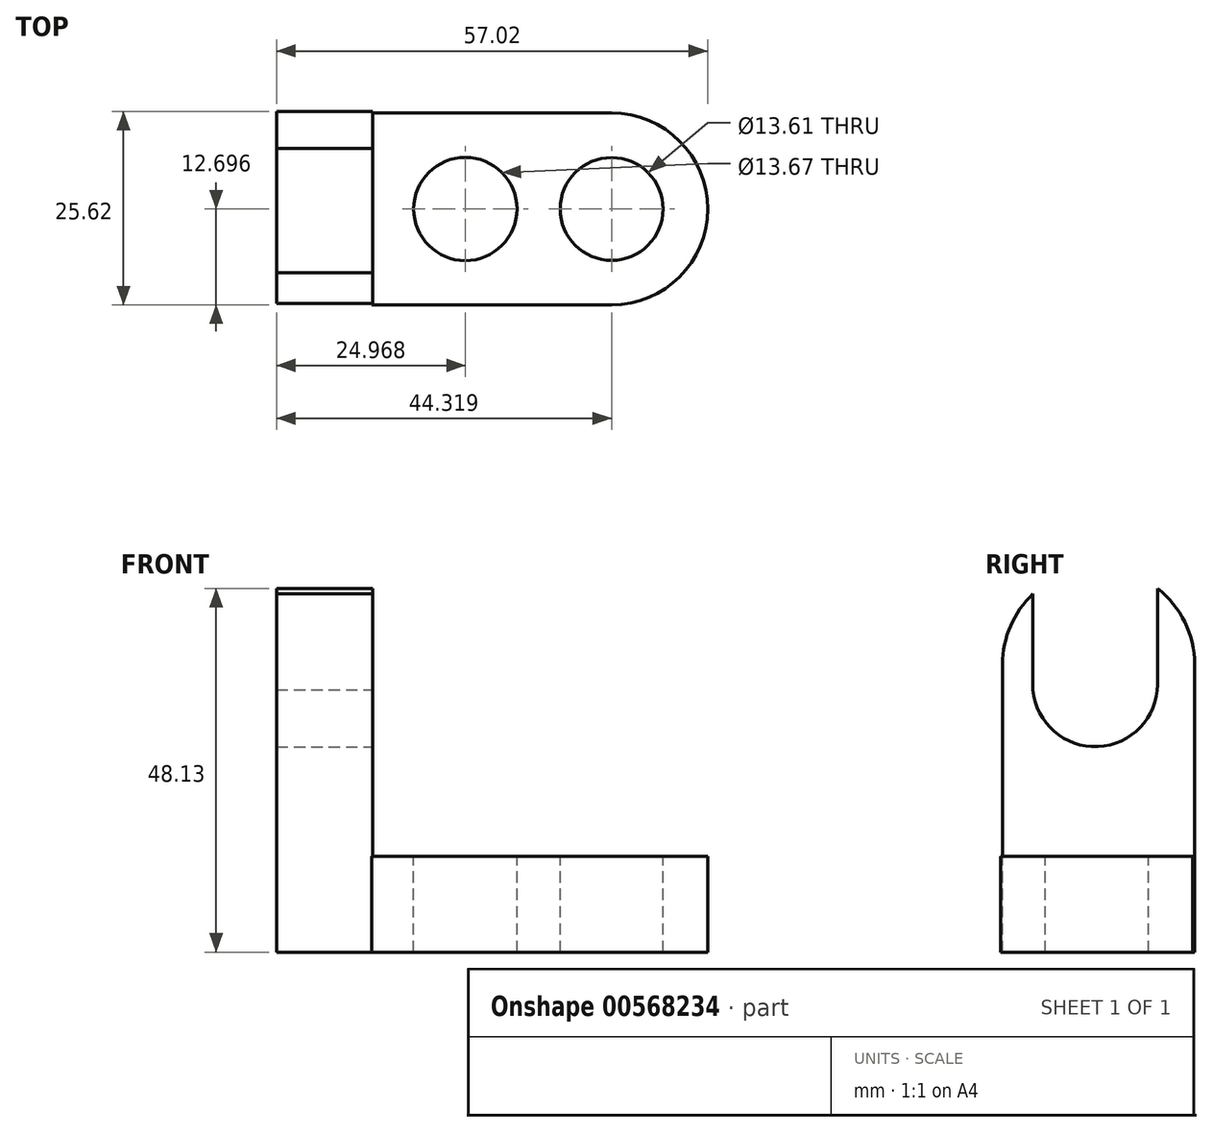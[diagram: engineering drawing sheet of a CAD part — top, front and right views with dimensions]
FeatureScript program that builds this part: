
annotation { "Feature Type Name" : "Feature", "Feature Type Description" : "" }
export const myFeature = defineFeature(function(context is Context, id is Id, definition is map)
    precondition{}
    {
        {
            var Q0;
            Q0=qCreatedBy(makeId("Right.planeOp"),FACE);
            var sketch = newSketch(context, id + "F0", { "sketchPlane" : qUnion([Q0])});
            skLineSegment(sketch, "E0", {"start": v(-51.63, 0) * mm, "end": v(-26.23, 0) * mm});
            skLineSegment(sketch, "E1", {"start": v(-26.23, 0) * mm, "end": v(-26.23, 38.1) * mm});
            skLineSegment(sketch, "E2", {"start": v(-26.23, 38.1) * mm, "end": v(-51.63, 38.1) * mm});
            skLineSegment(sketch, "E3", {"start": v(-51.63, 38.1) * mm, "end": v(-51.63, 0) * mm});
            skArc(sketch, "E4", {"start": v(-26.23, 38.1) * mm, "mid": v(-38.93, 50.8) * mm, "end": v(-51.63, 38.1) * mm});
            skSolve(sketch);
        }
        {
            var Q0;
            Q0=makeQuery(id+"F0.imprint","IMPRINT",FACE,{"disambiguationData":[TD([[makeQuery(id+"F0.imprint","IMPRINT",EDGE,{"derivedFrom":sQuery(id+"F0.wireOp",EDGE,"E0")}),1.0]])]});
            var Q1;
            Q1=makeQuery(id+"F0.imprint","IMPRINT",FACE,{"disambiguationData":[TD([[makeQuery(id+"F0.imprint","IMPRINT",EDGE,{"derivedFrom":sQuery(id+"F0.wireOp",EDGE,"E2")}),-1.0]])]});
            extrude(context, id + "F1", {"entities" : qUnion([Q0, Q1]), "depth" : 12.7 * mm, "offsetDistance" : 25.4 * mm});
        }
        {
            var Q0;
            Q0=qCreatedBy(makeId("Top.planeOp"),FACE);
            var sketch = newSketch(context, id + "F2", { "sketchPlane" : qUnion([Q0])});
            skLineSegment(sketch, "E5", {"start": v(12.57, -26.45) * mm, "end": v(44.32, -26.45) * mm});
            skLineSegment(sketch, "E6", {"start": v(44.32, -26.45) * mm, "end": v(44.32, -51.85) * mm});
            skLineSegment(sketch, "E7", {"start": v(44.32, -51.85) * mm, "end": v(12.57, -51.85) * mm});
            skLineSegment(sketch, "E8", {"start": v(12.57, -51.85) * mm, "end": v(12.57, -26.45) * mm});
            skArc(sketch, "E9", {"start": v(44.32, -51.85) * mm, "mid": v(57.02, -39.15) * mm, "end": v(44.32, -26.45) * mm});
            skSolve(sketch);
        }
        {
            var Q0;
            Q0=makeQuery(id+"F2.imprint","IMPRINT",FACE,{"disambiguationData":[TD([[makeQuery(id+"F2.imprint","IMPRINT",EDGE,{"derivedFrom":sQuery(id+"F2.wireOp",EDGE,"E6")}),1.0]])]});
            var Q1;
            Q1=makeQuery(id+"F2.imprint","IMPRINT",FACE,{"disambiguationData":[TD([[makeQuery(id+"F2.imprint","IMPRINT",EDGE,{"derivedFrom":sQuery(id+"F2.wireOp",EDGE,"E5")}),-1.0]])]});
            extrude(context, id + "F3", {"entities" : qUnion([Q0, Q1]), "operationType" : NewBodyOperationType.ADD, "depth" : 12.7 * mm, "offsetDistance" : 25.4 * mm});
        }
        {
            var Q0;
            Q0=makeQuery(id+"F1.opExtrude","CAP_FACE",FACE,{"disambiguationData":[OSD([sQuery(id+"F0.wireOp",EDGE,"E0"),sQuery(id+"F0.wireOp",EDGE,"E1"),sQuery(id+"F0.wireOp",EDGE,"E3"),sQuery(id+"F0.wireOp",EDGE,"E4")])],"isStart":false});
            var sketch = newSketch(context, id + "F4", { "sketchPlane" : qUnion([Q0])});
            skLineSegment(sketch, "E10", {"start": v(-47.6, 47.38) * mm, "end": v(-47.6, 34.68) * mm});
            skLineSegment(sketch, "E11", {"start": v(-31.14, 48.13) * mm, "end": v(-31.14, 35.43) * mm});
            skArc(sketch, "E12", {"start": v(-47.6, 34.68) * mm, "mid": v(-39, 27.2) * mm, "end": v(-31.14, 35.43) * mm});
            skArc(sketch, "E13", {"start": v(-31.14, 48.13) * mm, "mid": v(-39.76, 56.37) * mm, "end": v(-47.6, 47.38) * mm});
            skSolve(sketch);
        }
        {
            var Q0;
            {var subQ0=sQuery(id+"F4.wireOp",EDGE,"E13");Q0=makeQuery(id+"F4.imprint","IMPRINT",FACE,{"disambiguationData":[TD([[makeQuery(id+"F4.imprint","IMPRINT",EDGE,{"derivedFrom":subQ0}),1.0]])]});}
            var Q1;
            {var subQ0=sQuery(id+"F4.wireOp",EDGE,"E10");Q1=makeQuery(id+"F4.imprint","IMPRINT",FACE,{"disambiguationData":[TD([[makeQuery(id+"F4.imprint","IMPRINT",EDGE,{"derivedFrom":subQ0}),1.0]])]});}
            extrude(context, id + "F5", {"entities" : qUnion([Q0, Q1]), "operationType" : NewBodyOperationType.REMOVE, "oppositeDirection" : true, "depth" : 12.7 * mm, "offsetDistance" : 25.4 * mm});
        }
        {
            var Q0;
            Q0=makeQuery(id+"F3.opExtrude","CAP_FACE",FACE,{"disambiguationData":[OSD([sQuery(id+"F2.wireOp",EDGE,"E5"),sQuery(id+"F2.wireOp",EDGE,"E7"),sQuery(id+"F2.wireOp",EDGE,"E8"),sQuery(id+"F2.wireOp",EDGE,"E9")])],"isStart":false});
            var sketch = newSketch(context, id + "F6", { "sketchPlane" : qUnion([Q0])});
            skCircle(sketch, "E14", {"center": v(44.32, -39.15) * mm, "radius": 6.8 * mm});
            skCircle(sketch, "E15", {"center": v(24.97, -39.15) * mm, "radius": 6.83 * mm});
            skSolve(sketch);
        }
        {
            var Q0;
            Q0=makeQuery(id+"F6.imprint","IMPRINT",FACE,{"disambiguationData":[TD([[makeQuery(id+"F6.imprint","IMPRINT",EDGE,{"derivedFrom":sQuery(id+"F6.wireOp",EDGE,"E15")}),1.0]])]});
            var Q1;
            Q1=makeQuery(id+"F6.imprint","IMPRINT",FACE,{"disambiguationData":[TD([[makeQuery(id+"F6.imprint","IMPRINT",EDGE,{"derivedFrom":sQuery(id+"F6.wireOp",EDGE,"E14")}),1.0]])]});
            extrude(context, id + "F7", {"entities" : qUnion([Q0, Q1]), "operationType" : NewBodyOperationType.REMOVE, "oppositeDirection" : true, "depth" : 12.7 * mm, "offsetDistance" : 25.4 * mm});
        }
    });
